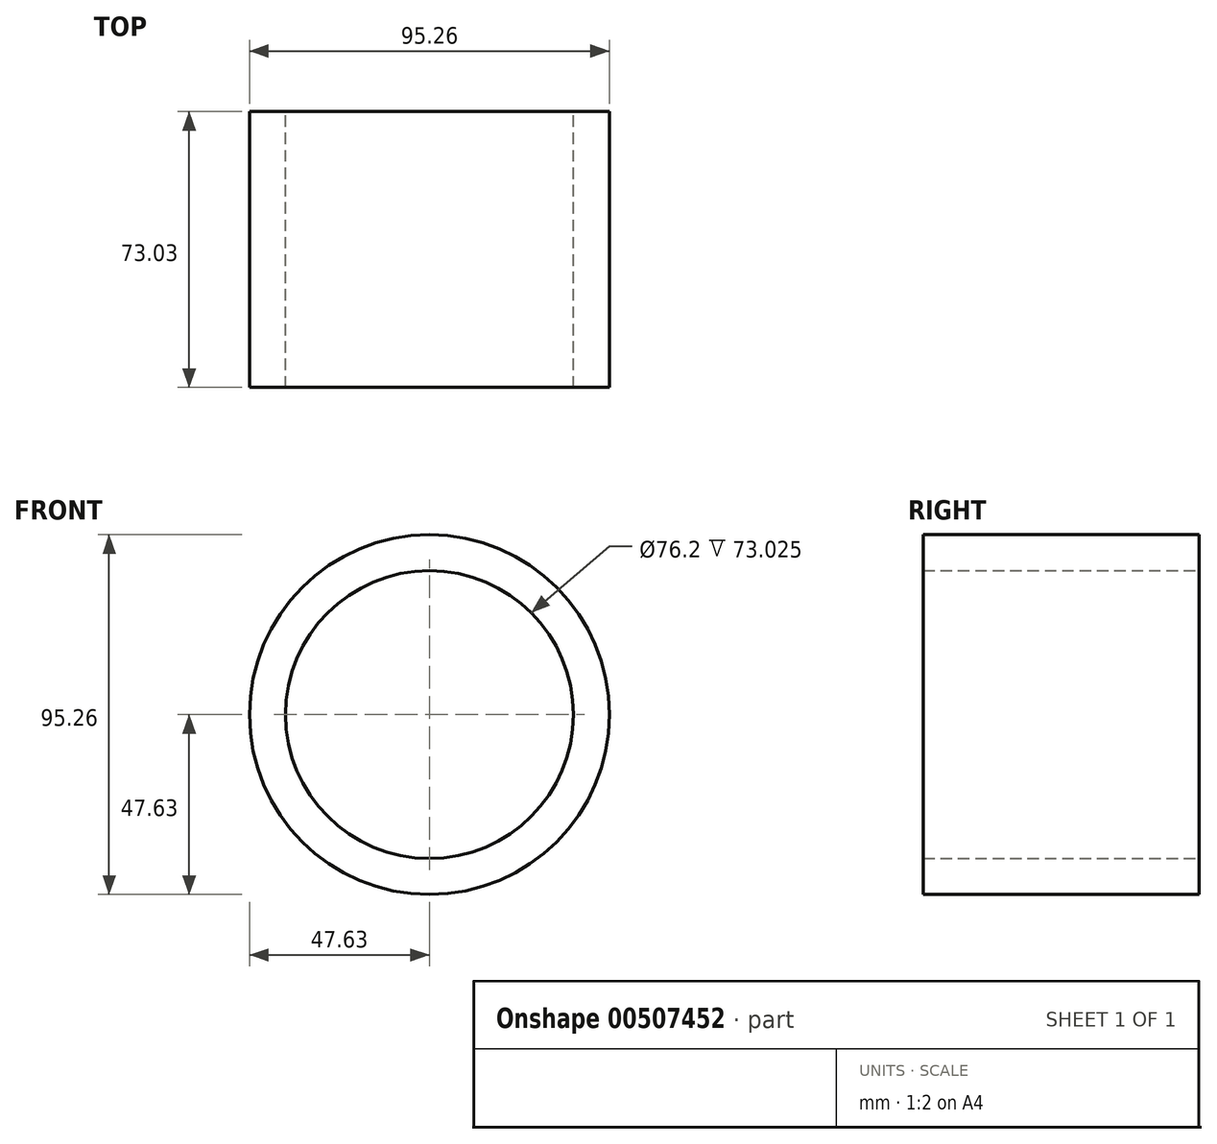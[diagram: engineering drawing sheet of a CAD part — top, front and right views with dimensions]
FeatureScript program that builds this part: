
annotation { "Feature Type Name" : "Feature", "Feature Type Description" : "" }
export const myFeature = defineFeature(function(context is Context, id is Id, definition is map)
    precondition{}
    {
        {
            var Q0;
            Q0=qCreatedBy(makeId("Front.planeOp"),FACE);
            var sketch = newSketch(context, id + "F0", { "sketchPlane" : qUnion([Q0])});
            skCircle(sketch, "E0", {"center": v(0, 0) * mm, "radius": 38.1 * mm});
            skCircle(sketch, "E1", {"center": v(0, 0) * mm, "radius": 47.63 * mm});
            skSolve(sketch);
        }
        {
            var Q0;
            Q0=makeQuery(id+"F0.imprint","IMPRINT",FACE,{"disambiguationData":[TD([[makeQuery(id+"F0.imprint","IMPRINT",EDGE,{"derivedFrom":sQuery(id+"F0.wireOp",EDGE,"E0")}),-1.0]])]});
            extrude(context, id + "F1", {"entities" : qUnion([Q0]), "depth" : 73.02 * mm});
        }
    });
